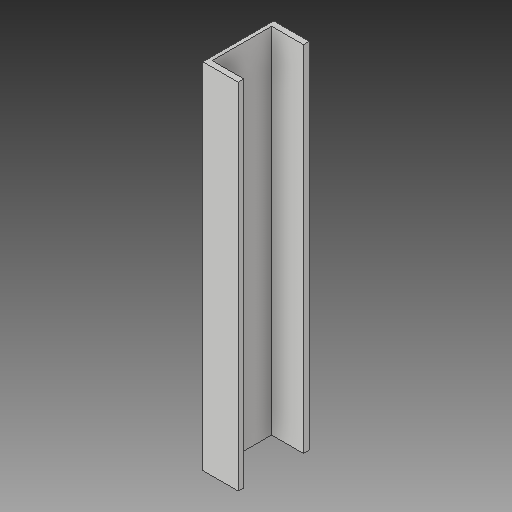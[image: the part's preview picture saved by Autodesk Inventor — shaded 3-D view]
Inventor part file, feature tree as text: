
AUTODESK INVENTOR PART (.ipt)
format: ipt  version: 2019 (Build 230136000, 136)  size: 89,088 bytes
history: native  units: mm
features: extrude x1, sketch x1
ambient origin geometry x8: Origin, YZ Plane, XZ Plane, XY Plane, X Axis, Y Axis, Z Axis, Center Point
bodies: Solid1 (feature_tree)
feature tree (2):
  extrude  "Extrusion1"  Depth=100.0mm
  sketch  "Sketch1"  dims[d0=50.0mm d1=100.0mm d2=8.0mm d3=45.0mm d4=84.0mm d5=500.0mm d6=0.0mm]
